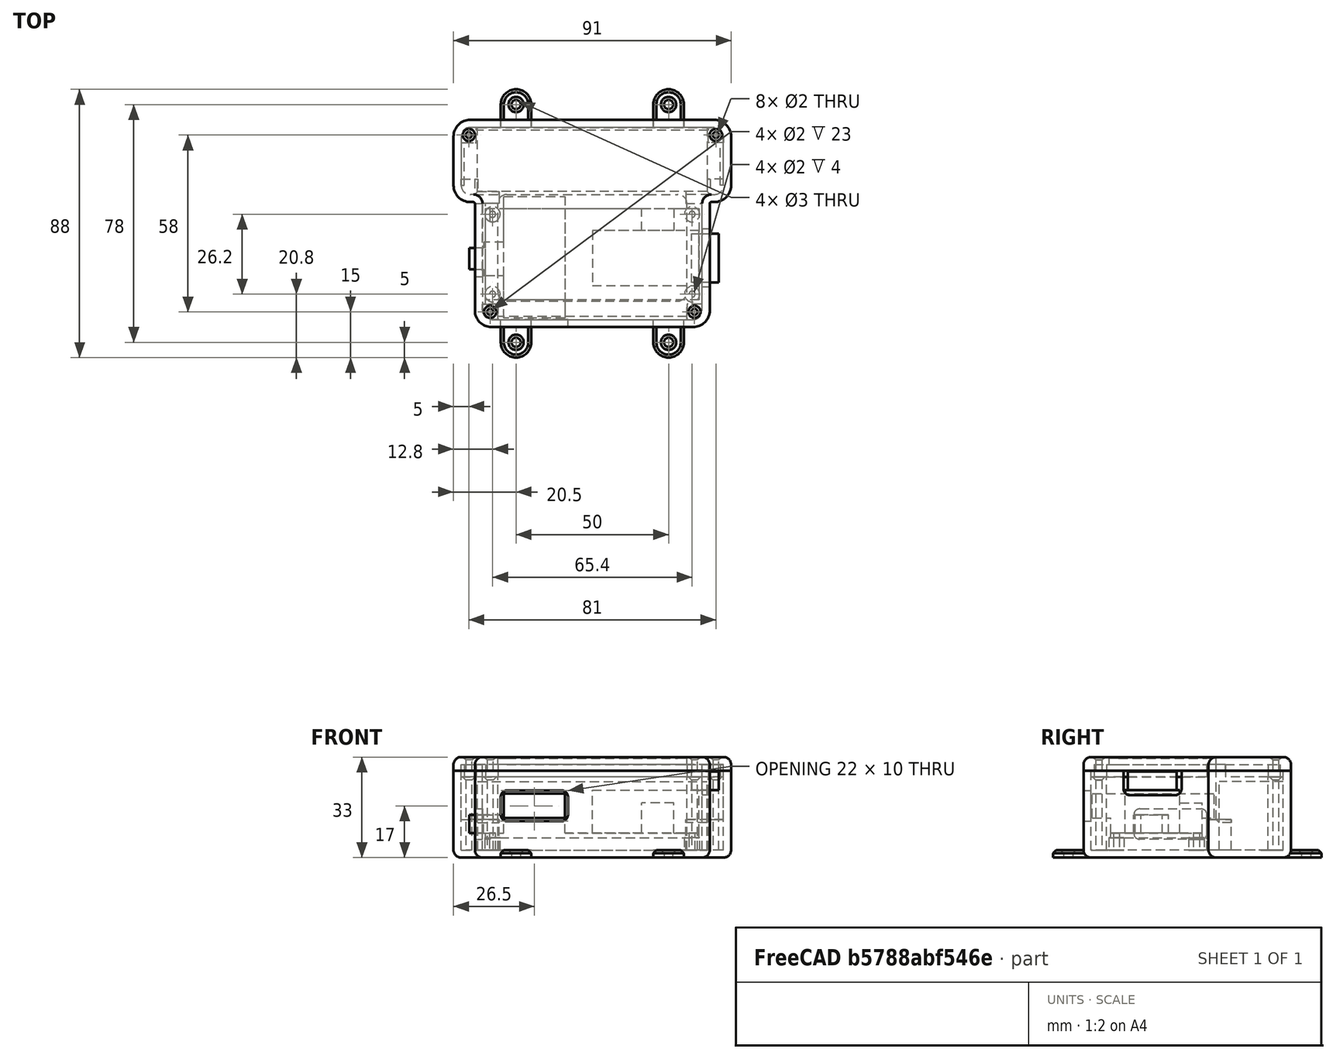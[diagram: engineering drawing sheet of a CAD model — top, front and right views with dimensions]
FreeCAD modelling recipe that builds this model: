
FCSTD DOCUMENT  (FreeCAD 0.18R16110 (Git))
Label: Boitier_elec_V1
License: All rights reserved
LicenseURL: http://en.wikipedia.org/wiki/All_rights_reserved
objects: Sketcher::SketchObject×21, PartDesign::Pad×16, PartDesign::Fillet×5, PartDesign::Pocket×5, PartDesign::Body×4, PartDesign::Chamfer×4, PartDesign::Thickness×2, Mesh::Feature×2
note: 78 computed .brp shape members not serialized (recipe doc carries the construction recipe); baked Part::Feature solids carry a one-line shape summary decoded from their .brp

FEATURE [Sketcher::SketchObject] Sketch
  MapMode = 5
  Support = -> [XY_Plane]
  sketch-geometry (8):
    g0: LineSegment StartX=-43 StartY=22 StartZ=0 EndX=-43 EndY=0 EndZ=0
    g1: LineSegment StartX=-43 StartY=0 StartZ=0 EndX=-36 EndY=0 EndZ=0
    g2: LineSegment StartX=-36 StartY=0 StartZ=0 EndX=-36 EndY=-41 EndZ=0
    g3: LineSegment StartX=-36 StartY=-41 StartZ=0 EndX=36 EndY=-41 EndZ=0
    g4: LineSegment StartX=36 StartY=-41 StartZ=0 EndX=36 EndY=0 EndZ=0
    g5: LineSegment StartX=36 StartY=0 StartZ=0 EndX=43 EndY=0 EndZ=0
    g6: LineSegment StartX=43 StartY=0 StartZ=0 EndX=43 EndY=22 EndZ=0
    g7: LineSegment StartX=43 StartY=22 StartZ=0 EndX=-43 EndY=22 EndZ=0
  constraints (22):
    c: Vertical(g0)
    c: Coincident(g0,g1)
    c: Horizontal(g1)
    c: Coincident(g1,g2)
    c: Vertical(g2)
    c: Coincident(g2,g3)
    c: Coincident(g3,g4)
    c: Vertical(g4)
    c: Coincident(g4,g5)
    c: Horizontal(g5)
    c: Coincident(g5,g6)
    c: Vertical(g6)
    c: Coincident(g6,g7)
    c: Coincident(g7,g0)
    c: Symmetric(g0,g6,g-2)
    c: Symmetric(g2,g3,g-2)
    c: DistanceX(g3,g3) = 72
    c: DistanceY(g4,g4) = 41
    c: Equal(g2,g4)
    c: DistanceX(g7,g7) = 86
    c: DistanceY(g6,g6) = 22
    c: PointOnObject(g1,g-1)
FEATURE [PartDesign::Pad] Pad  label="Contours_boite"
  Length = 26
  Length2 = 100
  Profile = -> Sketch
  Type = 0
FEATURE [PartDesign::Fillet] Fillet
  Base = -> Pad [Edge8,Edge11,Edge17,Edge2,Edge1,Edge20,Edge14,Edge5]
  BaseFeature = -> Pad
  Radius = 3
FEATURE [PartDesign::Thickness] Thickness
  Base = -> Fillet [Face5]
  BaseFeature = -> Fillet
  Join = 0
  Mode = 0
  Value = 2.5
FEATURE [Sketcher::SketchObject] Sketch001
  ExternalGeometry = -> [Thickness]
  MapMode = 5
  Support = -> [Thickness]
  sketch-geometry (8):
    g0: Circle CenterX=-32.7 CenterY=-6.5 CenterZ=0 NormalX=0 NormalY=0 NormalZ=1 AngleXU=0 Radius=1
    g1: Circle CenterX=-32.7 CenterY=-32.7 CenterZ=0 NormalX=0 NormalY=0 NormalZ=1 AngleXU=0 Radius=1
    g2: Circle CenterX=32.7 CenterY=-6.5 CenterZ=0 NormalX=0 NormalY=0 NormalZ=1 AngleXU=0 Radius=1
    g3: Circle CenterX=32.7 CenterY=-32.7 CenterZ=0 NormalX=0 NormalY=0 NormalZ=1 AngleXU=0 Radius=1
    g4: Circle CenterX=-32.7 CenterY=-6.5 CenterZ=0 NormalX=0 NormalY=0 NormalZ=1 AngleXU=0 Radius=2.5
    g5: Circle CenterX=-32.7 CenterY=-32.7 CenterZ=0 NormalX=0 NormalY=0 NormalZ=1 AngleXU=0 Radius=2.5
    g6: Circle CenterX=32.7 CenterY=-32.7 CenterZ=0 NormalX=0 NormalY=0 NormalZ=1 AngleXU=0 Radius=2.5
    g7: Circle CenterX=32.7 CenterY=-6.5 CenterZ=0 NormalX=0 NormalY=0 NormalZ=1 AngleXU=0 Radius=2.5
  constraints (18):
    c: Symmetric(g0,g2,g-2)
    c: Symmetric(g1,g3,g-2)
    c: Radius(g0) = 1
    c: Equal(g0,g2)
    c: Equal(g0,g3)
    c: Equal(g0,g1)
    c: Distance(g1,g-4) = 8.3
    c: Distance(g0,g-4) = 34.5
    c: Distance(g1,g3) = 65.4
    c: Distance(g0,g2) = 65.4
    c: Coincident(g5,g1)
    c: Coincident(g6,g3)
    c: Coincident(g7,g2)
    c: Radius(g7) = 2.5
    c: Equal(g7,g6)
    c: Equal(g7,g4)
    c: Equal(g7,g5)
    c: Coincident(g4,g0)
FEATURE [PartDesign::Pad] Pad001  label="Piliers_fixation_PCB"
  BaseFeature = -> Thickness
  Length = 4
  Length2 = 100
  Profile = -> Sketch001
  Type = 0
FEATURE [Sketcher::SketchObject] Sketch002
  MapMode = 5
  Support = -> [XY_Plane001]
  sketch-geometry (8):
    g0: LineSegment StartX=-35 StartY=15 StartZ=0 EndX=35 EndY=15 EndZ=0
    g1: LineSegment StartX=35 StartY=15 StartZ=0 EndX=35 EndY=-15 EndZ=0
    g2: LineSegment StartX=35 StartY=-15 StartZ=0 EndX=-35 EndY=-15 EndZ=0
    g3: LineSegment StartX=-35 StartY=-15 StartZ=0 EndX=-35 EndY=15 EndZ=0
    g4: Circle CenterX=-32.7 CenterY=13.1 CenterZ=0 NormalX=0 NormalY=0 NormalZ=1 AngleXU=0 Radius=1
    g5: Circle CenterX=-32.7 CenterY=-13.1 CenterZ=0 NormalX=0 NormalY=0 NormalZ=1 AngleXU=0 Radius=1
    g6: Circle CenterX=32.7 CenterY=13.1 CenterZ=0 NormalX=0 NormalY=0 NormalZ=1 AngleXU=0 Radius=1
    g7: Circle CenterX=32.7 CenterY=-13.1 CenterZ=0 NormalX=0 NormalY=0 NormalZ=1 AngleXU=0 Radius=1
  constraints (19):
    c: Coincident(g0,g1)
    c: Coincident(g1,g2)
    c: Coincident(g2,g3)
    c: Coincident(g3,g0)
    c: Horizontal(g2)
    c: Vertical(g1)
    c: DistanceY(g1,g1) = 30
    c: DistanceX(g0,g0) = 70
    c: Symmetric(g0,g0,g-2)
    c: Radius(g4) = 1
    c: Equal(g4,g5)
    c: Equal(g4,g6)
    c: Equal(g4,g7)
    c: Distance(g4,g5) = 26.2
    c: Symmetric(g4,g6,g-2)
    c: Distance(g4,g6) = 65.4
    c: Symmetric(g5,g7,g-2)
    c: Symmetric(g2,g0,g-1)
    c: Symmetric(g7,g6,g-1)
FEATURE [PartDesign::Pad] Pad002
  Length = 1.5
  Length2 = 100
  Profile = -> Sketch002
  Type = 0
FEATURE [Sketcher::SketchObject] Sketch003
  ExternalGeometry = -> [Pad002]
  MapMode = 5
  Placement = pos=(0,0,1.5) rot=(0,0,1;0rad)
  Support = -> [Pad002]
  sketch-geometry (4):
    g0: LineSegment StartX=-29 StartY=15 StartZ=0 EndX=-9 EndY=15 EndZ=0
    g1: LineSegment StartX=-9 StartY=15 StartZ=0 EndX=-9 EndY=-15 EndZ=0
    g2: LineSegment StartX=-9 StartY=-15 StartZ=0 EndX=-29 EndY=-15 EndZ=0
    g3: LineSegment StartX=-29 StartY=-15 StartZ=0 EndX=-29 EndY=15 EndZ=0
  constraints (12):
    c: Coincident(g0,g1)
    c: Coincident(g1,g2)
    c: Coincident(g2,g3)
    c: Coincident(g3,g0)
    c: Horizontal(g0)
    c: Horizontal(g2)
    c: Vertical(g1)
    c: Vertical(g3)
    c: PointOnObject(g0,g-4)
    c: PointOnObject(g1,g-5)
    c: DistanceX(g2,g2) = 20
    c: Distance(g0,g-3) = 6
FEATURE [PartDesign::Pad] Pad003
  BaseFeature = -> Pad002
  Length = 5
  Length2 = 100
  Profile = -> Sketch003
  Type = 0
FEATURE [Sketcher::SketchObject] Sketch004
  ExternalGeometry = -> [Pad003]
  MapMode = 5
  Placement = pos=(0,0,6.5) rot=(0,0,1;0rad)
  Support = -> [Pad003]
  sketch-geometry (4):
    g0: LineSegment StartX=-29 StartY=19 StartZ=0 EndX=-9 EndY=19 EndZ=0
    g1: LineSegment StartX=-9 StartY=19 StartZ=0 EndX=-9 EndY=-21 EndZ=0
    g2: LineSegment StartX=-9 StartY=-21 StartZ=0 EndX=-29 EndY=-21 EndZ=0
    g3: LineSegment StartX=-29 StartY=-21 StartZ=0 EndX=-29 EndY=19 EndZ=0
  constraints (12):
    c: Coincident(g0,g1)
    c: Coincident(g1,g2)
    c: Coincident(g2,g3)
    c: Coincident(g3,g0)
    c: Horizontal(g0)
    c: Horizontal(g2)
    c: Vertical(g1)
    c: Vertical(g3)
    c: PointOnObject(g-6,g1)
    c: PointOnObject(g-4,g3)
    c: DistanceY(g1,g1) = 40
    c: Distance(g2,g-5) = 6
FEATURE [PartDesign::Pad] Pad004
  BaseFeature = -> Pad003
  Length = 8
  Length2 = 100
  Profile = -> Sketch004
  Type = 0
FEATURE [Sketcher::SketchObject] Sketch005
  ExternalGeometry = -> [Pad004]
  MapMode = 5
  Placement = pos=(0,0,1.5) rot=(0,0,1;0rad)
  Support = -> [Pad004]
  sketch-geometry (4):
    g0: LineSegment StartX=35 StartY=7.7 StartZ=0 EndX=0 EndY=7.7 EndZ=0
    g1: LineSegment StartX=0 StartY=7.7 StartZ=0 EndX=0 EndY=-10.3 EndZ=0
    g2: LineSegment StartX=0 StartY=-10.3 StartZ=0 EndX=35 EndY=-10.3 EndZ=0
    g3: LineSegment StartX=35 StartY=-10.3 StartZ=0 EndX=35 EndY=7.7 EndZ=0
  constraints (12):
    c: Coincident(g0,g1)
    c: Coincident(g1,g2)
    c: Coincident(g2,g3)
    c: Coincident(g3,g0)
    c: Horizontal(g0)
    c: Horizontal(g2)
    c: Vertical(g1)
    c: Vertical(g3)
    c: PointOnObject(g0,g-4)
    c: DistanceY(g3,g3) = 18
    c: DistanceX(g2,g2) = 35
    c: Distance(g1,g-5) = 4.7
FEATURE [PartDesign::Pad] Pad005
  BaseFeature = -> Pad004
  Length = 14.2
  Length2 = 100
  Profile = -> Sketch005
  Type = 0
FEATURE [Sketcher::SketchObject] Sketch006
  ExternalGeometry = -> [Pad005]
  MapMode = 5
  Placement = pos=(0,0,15.7) rot=(0,0,1;0rad)
  Support = -> [Pad005]
  sketch-geometry (4):
    g0: LineSegment StartX=32.5 StartY=6.7 StartZ=0 EndX=41.5 EndY=6.7 EndZ=0
    g1: LineSegment StartX=41.5 StartY=6.7 StartZ=0 EndX=41.5 EndY=-9.3 EndZ=0
    g2: LineSegment StartX=41.5 StartY=-9.3 StartZ=0 EndX=32.5 EndY=-9.3 EndZ=0
    g3: LineSegment StartX=32.5 StartY=-9.3 StartZ=0 EndX=32.5 EndY=6.7 EndZ=0
  constraints (12):
    c: Coincident(g0,g1)
    c: Coincident(g1,g2)
    c: Coincident(g2,g3)
    c: Coincident(g3,g0)
    c: Horizontal(g0)
    c: Horizontal(g2)
    c: Vertical(g1)
    c: Vertical(g3)
    c: DistanceY(g3,g3) = 16
    c: Distance(g0,g-3) = 1
    c: Distance(g0,g-5) = 2.5
    c: DistanceX(g2,g2) = 9
FEATURE [PartDesign::Pad] Pad006
  BaseFeature = -> Pad005
  Length = 6
  Length2 = 100
  Profile = -> Sketch006
  Type = 0
FEATURE [Sketcher::SketchObject] Sketch007
  ExternalGeometry = -> [Pad001]
  MapMode = 5
  Placement = pos=(38.5,0,0) rot=(0.57735,0.57735,0.57735;2.0944rad)
  Support = -> [Pad001]
  sketch-geometry (4):
    g0: LineSegment StartX=-30.35 StartY=26 StartZ=0 EndX=-11.35 EndY=26 EndZ=0
    g1: LineSegment StartX=-11.35 StartY=26 StartZ=0 EndX=-11.35 EndY=18 EndZ=0
    g2: LineSegment StartX=-11.35 StartY=18 StartZ=0 EndX=-30.35 EndY=18 EndZ=0
    g3: LineSegment StartX=-30.35 StartY=18 StartZ=0 EndX=-30.35 EndY=26 EndZ=0
  constraints (12):
    c: Coincident(g0,g1)
    c: Coincident(g1,g2)
    c: Coincident(g2,g3)
    c: Coincident(g3,g0)
    c: Horizontal(g0)
    c: Horizontal(g2)
    c: Vertical(g1)
    c: Vertical(g3)
    c: PointOnObject(g0,g-3)
    c: DistanceX(g2,g2) = 19
    c: DistanceY(g3,g3) = 8
    c: Distance(g0,g-4) = 7.65
FEATURE [PartDesign::Pocket] Pocket  label="Passage_fils_prog"
  BaseFeature = -> Pad001
  Length = 5
  Length2 = 100
  Profile = -> Sketch007
  Type = 0
FEATURE [Sketcher::SketchObject] Sketch008
  MapMode = 5
  Support = -> [XY_Plane002]
  sketch-geometry (4):
    g0: LineSegment StartX=-37.625 StartY=22 StartZ=0 EndX=37.625 EndY=22 EndZ=0
    g1: LineSegment StartX=37.625 StartY=22 StartZ=0 EndX=37.625 EndY=1 EndZ=0
    g2: LineSegment StartX=37.625 StartY=1 StartZ=0 EndX=-37.625 EndY=1 EndZ=0
    g3: LineSegment StartX=-37.625 StartY=1 StartZ=0 EndX=-37.625 EndY=22 EndZ=0
  constraints (11):
    c: Coincident(g0,g1)
    c: Coincident(g1,g2)
    c: Coincident(g2,g3)
    c: Coincident(g3,g0)
    c: Horizontal(g2)
    c: Vertical(g1)
    c: Vertical(g3)
    c: Symmetric(g0,g0,g-2)
    c: DistanceY(g1,g1) = 21
    c: DistanceX(g0,g0) = 75.25
    c: DistanceY(g-1,g0) = 22
FEATURE [PartDesign::Pad] Pad007
  Length = 22.5
  Length2 = 100
  Profile = -> Sketch008
  Type = 0
FEATURE [PartDesign::Body] Body002  label="Porte_batterie"
  Group = -> [Sketch008,Pad007]
  Origin = -> Origin002
  Tip = -> Pad007
FEATURE [Sketcher::SketchObject] Sketch009
  ExternalGeometry = -> [Pocket]
  MapMode = 5
  Support = -> [Pocket]
  sketch-geometry (14):
    g0: LineSegment StartX=43 StartY=5 StartZ=0 EndX=37.6 EndY=5 EndZ=0
    g1: LineSegment StartX=37.6 StartY=5 StartZ=0 EndX=37.6 EndY=1 EndZ=0
    g2: LineSegment StartX=37.6 StartY=1 StartZ=0 EndX=30.6 EndY=1 EndZ=0
    g3: LineSegment StartX=30.6 StartY=1 StartZ=0 EndX=30.6 EndY=-3 EndZ=0
    g4: LineSegment StartX=30.6 StartY=-3 StartZ=0 EndX=37.6 EndY=-3 EndZ=0
    g5: LineSegment StartX=37.6 StartY=-3 StartZ=0 EndX=43 EndY=0 EndZ=0
    g6: LineSegment StartX=43 StartY=0 StartZ=0 EndX=43 EndY=5 EndZ=0
    g7: LineSegment StartX=-43 StartY=5 StartZ=0 EndX=-37.6 EndY=5 EndZ=0
    g8: LineSegment StartX=-37.6 StartY=5 StartZ=0 EndX=-37.6 EndY=1 EndZ=0
    g9: LineSegment StartX=-37.6 StartY=1 StartZ=0 EndX=-30.6 EndY=1 EndZ=0
    g10: LineSegment StartX=-30.6 StartY=1 StartZ=0 EndX=-30.6 EndY=-3 EndZ=0
    g11: LineSegment StartX=-30.6 StartY=-3 StartZ=0 EndX=-37.6 EndY=-3 EndZ=0
    g12: LineSegment StartX=-37.6 StartY=-3 StartZ=0 EndX=-43 EndY=0 EndZ=0
    g13: LineSegment StartX=-43 StartY=0 StartZ=0 EndX=-43 EndY=5 EndZ=0
  constraints (37):
    c: Horizontal(g0)
    c: Coincident(g0,g1)
    c: Vertical(g1)
    c: Coincident(g1,g2)
    c: Horizontal(g2)
    c: Coincident(g2,g3)
    c: Vertical(g3)
    c: Coincident(g3,g4)
    c: Horizontal(g4)
    c: Coincident(g4,g5)
    c: PointOnObject(g5,g-1)
    c: Coincident(g5,g6)
    c: Coincident(g6,g0)
    c: Vertical(g6)
    c: DistanceY(g3,g3) = 4
    c: DistanceX(g2,g2) = 7
    c: DistanceX(g0,g0) = 5.4
    c: DistanceY(g1,g1) = 4
    c: Distance(g0,g-1) = 5
    c: DistanceX(g4,g4) = 7
    c: PointOnObject(g0,g-5)
    c: Coincident(g7,g8)
    c: Coincident(g8,g9)
    c: Horizontal(g9)
    c: Coincident(g9,g10)
    c: Vertical(g10)
    c: Coincident(g10,g11)
    c: Coincident(g11,g12)
    c: PointOnObject(g12,g-1)
    c: Coincident(g12,g13)
    c: Coincident(g13,g7)
    c: Vertical(g13)
    c: Symmetric(g7,g0,g-2)
    c: Symmetric(g7,g0,g-2)
    c: Symmetric(g8,g1,g-2)
    c: Symmetric(g10,g3,g-2)
    c: Symmetric(g11,g4,g-2)
FEATURE [PartDesign::Pad] Pad008  label="Maintiens_batterie"
  BaseFeature = -> Pocket
  Length = 10
  Length2 = 100
  Profile = -> Sketch009
  Type = 0
FEATURE [Sketcher::SketchObject] Sketch010
  ExternalGeometry = -> [Pad006]
  MapMode = 5
  Placement = pos=(0,0,1.5) rot=(0,0,1;0rad)
  Support = -> [Pad006]
  sketch-geometry (4):
    g0: LineSegment StartX=16.2 StartY=15 StartZ=0 EndX=26.7 EndY=15 EndZ=0
    g1: LineSegment StartX=26.7 StartY=15 StartZ=0 EndX=26.7 EndY=7.7 EndZ=0
    g2: LineSegment StartX=26.7 StartY=7.7 StartZ=0 EndX=16.2 EndY=7.7 EndZ=0
    g3: LineSegment StartX=16.2 StartY=7.7 StartZ=0 EndX=16.2 EndY=15 EndZ=0
  constraints (12):
    c: Coincident(g0,g1)
    c: Coincident(g1,g2)
    c: Coincident(g2,g3)
    c: Coincident(g3,g0)
    c: Horizontal(g0)
    c: Horizontal(g2)
    c: Vertical(g1)
    c: Vertical(g3)
    c: PointOnObject(g0,g-3)
    c: PointOnObject(g1,g-5)
    c: Distance(g0,g-4) = 8.3
    c: DistanceX(g0,g0) = 10.5
FEATURE [PartDesign::Pad] Pad009
  BaseFeature = -> Pad006
  Length = 10
  Length2 = 100
  Profile = -> Sketch010
  Type = 0
FEATURE [Sketcher::SketchObject] Sketch012
  ExternalGeometry = -> [Pad009]
  MapMode = 5
  Placement = pos=(0,0,1.5) rot=(0,0,1;0rad)
  Support = -> [Pad009]
  sketch-geometry (8):
    g0: LineSegment StartX=-29 StartY=4 StartZ=0 EndX=-35.7 EndY=4 EndZ=0
    g1: LineSegment StartX=-35.7 StartY=4 StartZ=0 EndX=-35.7 EndY=2 EndZ=0
    g2: LineSegment StartX=-35.7 StartY=2 StartZ=0 EndX=-40.4 EndY=2 EndZ=0
    g3: LineSegment StartX=-40.4 StartY=2 StartZ=0 EndX=-40.4 EndY=-5 EndZ=0
    g4: LineSegment StartX=-40.4 StartY=-5 StartZ=0 EndX=-35.7 EndY=-5 EndZ=0
    g5: LineSegment StartX=-35.7 StartY=-5 StartZ=0 EndX=-35.7 EndY=-7 EndZ=0
    g6: LineSegment StartX=-35.7 StartY=-7 StartZ=0 EndX=-29 EndY=-7 EndZ=0
    g7: LineSegment StartX=-29 StartY=-7 StartZ=0 EndX=-29 EndY=4 EndZ=0
  constraints (24):
    c: PointOnObject(g0,g-6)
    c: Horizontal(g0)
    c: Coincident(g0,g1)
    c: Vertical(g1)
    c: Coincident(g1,g2)
    c: Horizontal(g2)
    c: Coincident(g2,g3)
    c: Vertical(g3)
    c: Coincident(g3,g4)
    c: Horizontal(g4)
    c: Coincident(g4,g5)
    c: Vertical(g5)
    c: Coincident(g5,g6)
    c: Horizontal(g6)
    c: Coincident(g6,g7)
    c: Coincident(g7,g0)
    c: Vertical(g7)
    c: DistanceX(g0,g0) = 6.7
    c: Equal(g0,g6)
    c: DistanceX(g2,g2) = 4.7
    c: DistanceY(g3,g3) = 7
    c: DistanceY(g5,g5) = 2
    c: Equal(g5,g1)
    c: Distance(g5,g-5) = 8
FEATURE [PartDesign::Pad] Pad010
  BaseFeature = -> Pad009
  Length = 6
  Length2 = 100
  Profile = -> Sketch012
  Type = 0
FEATURE [PartDesign::Body] Body001  label="PCB"
  Group = -> [Sketch002,Pad002,Sketch003,Pad003,Sketch004,Pad004,Sketch005,Pad005,Sketch006,Pad006,Sketch010,Pad009,Sketch012,Pad010]
  Origin = -> Origin001
  Placement = pos=(0,-19.6,4) rot=(0,0,1;0rad)
  Tip = -> Pad010
FEATURE [Sketcher::SketchObject] Sketch013
  MapMode = 5
  Placement = pos=(0,-43.5,0) rot=(1,0,0;1.5708rad)
  sketch-geometry (4):
    g0: LineSegment StartX=-30 StartY=19.5 StartZ=0 EndX=-8 EndY=19.5 EndZ=0
    g1: LineSegment StartX=-8 StartY=19.5 StartZ=0 EndX=-8 EndY=9.5 EndZ=0
    g2: LineSegment StartX=-8 StartY=9.5 StartZ=0 EndX=-30 EndY=9.5 EndZ=0
    g3: LineSegment StartX=-30 StartY=9.5 StartZ=0 EndX=-30 EndY=19.5 EndZ=0
  constraints (11):
    c: Coincident(g0,g1)
    c: Coincident(g1,g2)
    c: Coincident(g2,g3)
    c: Coincident(g3,g0)
    c: Horizontal(g0)
    c: Horizontal(g2)
    c: Vertical(g1)
    c: Vertical(g3)
    c: DistanceX(g2,g2) = 22
    c: DistanceY(g3,g3) = 10
    c: DistanceY(g-1,g2) = 9.5
FEATURE [PartDesign::Pocket] Pocket002  label="Passage_solar_usb"
  BaseFeature = -> Pad008
  Length = 5
  Length2 = 100
  Profile = -> Sketch013
  Type = 0
FEATURE [Sketcher::SketchObject] Sketch014
  ExternalGeometry = -> [Pocket002]
  MapMode = 5
  Placement = pos=(-38.5,0,0) rot=(0.57735,-0.57735,-0.57735;2.0944rad)
  Support = -> [Pocket002]
  sketch-geometry (4):
    g0: LineSegment StartX=3 StartY=13.5 StartZ=0 EndX=27 EndY=13.5 EndZ=0
    g1: LineSegment StartX=27 StartY=13.5 StartZ=0 EndX=27 EndY=3.5 EndZ=0
    g2: LineSegment StartX=27 StartY=3.5 StartZ=0 EndX=3 EndY=3.5 EndZ=0
    g3: LineSegment StartX=3 StartY=3.5 StartZ=0 EndX=3 EndY=13.5 EndZ=0
  constraints (12):
    c: Coincident(g0,g1)
    c: Coincident(g1,g2)
    c: Coincident(g2,g3)
    c: Coincident(g3,g0)
    c: Horizontal(g0)
    c: Horizontal(g2)
    c: Vertical(g1)
    c: Vertical(g3)
    c: PointOnObject(g0,g-3)
    c: DistanceX(g0,g0) = 24
    c: DistanceY(g1,g1) = 10
    c: DistanceY(g-1,g1) = 3.5
FEATURE [PartDesign::Pocket] Pocket003  label="Passage_fils_interrupteur"
  BaseFeature = -> Pocket002
  Length = 5
  Length2 = 100
  Profile = -> Sketch014
  Type = 0
FEATURE [PartDesign::Fillet] Fillet001
  Base = -> Pocket003 [Edge185,Edge187,Edge184,Edge186]
  BaseFeature = -> Pocket003
  Radius = 2
FEATURE [PartDesign::Fillet] Fillet002
  Base = -> Fillet001 [Edge205,Edge206,Edge204,Edge203]
  BaseFeature = -> Fillet001
  Radius = 2
FEATURE [PartDesign::Fillet] Fillet003
  Base = -> Fillet002 [Edge157,Edge200]
  BaseFeature = -> Fillet002
  Radius = 2
FEATURE [Sketcher::SketchObject] Sketch015
  ExternalGeometry = -> [Fillet003]
  MapMode = 5
  Support = -> [Fillet003]
  sketch-geometry (20):
    g0: LineSegment StartX=-43 StartY=17 StartZ=0 EndX=-38 EndY=17 EndZ=0
    g1: LineSegment StartX=-38 StartY=17 StartZ=0 EndX=-38 EndY=22 EndZ=0
    g2: LineSegment StartX=-38 StartY=22 StartZ=0 EndX=-43 EndY=22 EndZ=0
    g3: LineSegment StartX=-43 StartY=22 StartZ=0 EndX=-43 EndY=17 EndZ=0
    g4: Circle CenterX=-40.5 CenterY=19.5 CenterZ=0 NormalX=0 NormalY=0 NormalZ=1 AngleXU=0 Radius=1
    g5: LineSegment StartX=43 StartY=17 StartZ=0 EndX=38 EndY=17 EndZ=0
    g6: LineSegment StartX=38 StartY=17 StartZ=0 EndX=38 EndY=22 EndZ=0
    g7: LineSegment StartX=38 StartY=22 StartZ=0 EndX=43 EndY=22 EndZ=0
    g8: LineSegment StartX=43 StartY=22 StartZ=0 EndX=43 EndY=17 EndZ=0
    g9: Circle CenterX=40.5 CenterY=19.5 CenterZ=0 NormalX=0 NormalY=0 NormalZ=1 AngleXU=0 Radius=1
    g10: LineSegment StartX=31 StartY=-41 StartZ=0 EndX=36 EndY=-41 EndZ=0
    g11: LineSegment StartX=36 StartY=-41 StartZ=0 EndX=36 EndY=-36 EndZ=0
    g12: LineSegment StartX=36 StartY=-36 StartZ=0 EndX=31 EndY=-36 EndZ=0
    g13: LineSegment StartX=31 StartY=-36 StartZ=0 EndX=31 EndY=-41 EndZ=0
    g14: LineSegment StartX=-36 StartY=-36 StartZ=0 EndX=-31 EndY=-36 EndZ=0
    g15: LineSegment StartX=-31 StartY=-36 StartZ=0 EndX=-31 EndY=-41 EndZ=0
    g16: LineSegment StartX=-31 StartY=-41 StartZ=0 EndX=-36 EndY=-41 EndZ=0
    g17: LineSegment StartX=-36 StartY=-41 StartZ=0 EndX=-36 EndY=-36 EndZ=0
    g18: Circle CenterX=-33.5 CenterY=-38.5 CenterZ=0 NormalX=0 NormalY=0 NormalZ=1 AngleXU=0 Radius=1
    g19: Circle CenterX=33.5 CenterY=-38.5 CenterZ=0 NormalX=0 NormalY=0 NormalZ=1 AngleXU=0 Radius=1
  constraints (60):
    c: Coincident(g0,g1)
    c: Coincident(g1,g2)
    c: Coincident(g2,g3)
    c: Coincident(g3,g0)
    c: Horizontal(g0)
    c: Horizontal(g2)
    c: Vertical(g1)
    c: Vertical(g3)
    c: PointOnObject(g0,g-3)
    c: PointOnObject(g1,g-4)
    c: DistanceX(g0,g0) = 5
    c: DistanceY(g1,g1) = 5
    c: Distance(g4,g3) = 2.5
    c: Distance(g4,g2) = 2.5
    c: Coincident(g5,g6)
    c: Coincident(g6,g7)
    c: Coincident(g7,g8)
    c: Coincident(g8,g5)
    c: Horizontal(g5)
    c: Horizontal(g7)
    c: Vertical(g6)
    c: Vertical(g8)
    c: PointOnObject(g5,g-5)
    c: PointOnObject(g6,g-4)
    c: DistanceY(g8,g8) = 5
    c: DistanceX(g5,g5) = 5
    c: Distance(g9,g8) = 2.5
    c: Distance(g9,g7) = 2.5
    c: Coincident(g10,g11)
    c: Coincident(g11,g12)
    c: Coincident(g12,g13)
    c: Coincident(g13,g10)
    c: Horizontal(g10)
    c: Horizontal(g12)
    c: Vertical(g11)
    c: Vertical(g13)
    c: PointOnObject(g10,g-6)
    c: PointOnObject(g11,g-8)
    c: DistanceY(g13,g13) = 5
    c: DistanceX(g12,g12) = 5
    c: Coincident(g14,g15)
    c: Coincident(g15,g16)
    c: Coincident(g16,g17)
    c: Coincident(g17,g14)
    c: Horizontal(g14)
    c: Horizontal(g16)
    c: Vertical(g15)
    c: Vertical(g17)
    c: PointOnObject(g14,g-7)
    c: PointOnObject(g15,g-6)
    c: DistanceY(g15,g15) = 5
    c: DistanceX(g14,g14) = 5
    c: Distance(g18,g16) = 2.5
    c: Distance(g18,g17) = 2.5
    c: Distance(g19,g10) = 2.5
    c: Distance(g19,g11) = 2.5
    c: Radius(g19) = 1
    c: Equal(g19,g9)
    c: Equal(g19,g4)
    c: Equal(g19,g18)
FEATURE [PartDesign::Pad] Pad011
  BaseFeature = -> Fillet003
  Length = 24
  Length2 = 100
  Profile = -> Sketch015
  Type = 0
FEATURE [Sketcher::SketchObject] Sketch016
  ExternalGeometry = -> [Pad011]
  MapMode = 5
  Placement = pos=(0,0,-2.5) rot=(1,0,0;3.14159rad)
  Support = -> [Pad011]
  sketch-geometry (20):
    g0: ArcOfCircle CenterX=-25 CenterY=48.5 CenterZ=0 NormalX=0 NormalY=0 NormalZ=1 AngleXU=0 Radius=5 StartAngle=-1.2159e-12 EndAngle=3.14159
    g1: ArcOfCircle CenterX=-25 CenterY=38.5 CenterZ=0 NormalX=0 NormalY=0 NormalZ=1 AngleXU=0 Radius=5 StartAngle=3.14159 EndAngle=6.28319
    g2: LineSegment StartX=-30 StartY=48.5 StartZ=0 EndX=-30 EndY=38.5 EndZ=0
    g3: LineSegment StartX=-20 StartY=48.5 StartZ=0 EndX=-20 EndY=38.5 EndZ=0
    g4: Circle CenterX=-25 CenterY=48.5 CenterZ=0 NormalX=0 NormalY=0 NormalZ=1 AngleXU=0 Radius=1.5
    g5: ArcOfCircle CenterX=25 CenterY=48.5 CenterZ=0 NormalX=0 NormalY=0 NormalZ=1 AngleXU=0 Radius=5 StartAngle=1.00045e-11 EndAngle=3.14159
    g6: ArcOfCircle CenterX=25 CenterY=38.5 CenterZ=0 NormalX=0 NormalY=0 NormalZ=1 AngleXU=0 Radius=5 StartAngle=3.14159 EndAngle=6.28319
    g7: LineSegment StartX=20 StartY=48.5 StartZ=0 EndX=20 EndY=38.5 EndZ=0
    g8: LineSegment StartX=30 StartY=48.5 StartZ=0 EndX=30 EndY=38.5 EndZ=0
    g9: Circle CenterX=25 CenterY=48.5 CenterZ=0 NormalX=0 NormalY=0 NormalZ=1 AngleXU=0 Radius=1.5
    g10: ArcOfCircle CenterX=-25 CenterY=-19.5 CenterZ=0 NormalX=0 NormalY=0 NormalZ=1 AngleXU=0 Radius=5 StartAngle=6.867e-13 EndAngle=3.14159
    g11: ArcOfCircle CenterX=-25 CenterY=-29.5 CenterZ=0 NormalX=0 NormalY=0 NormalZ=1 AngleXU=0 Radius=5 StartAngle=3.14159 EndAngle=6.28319
    g12: LineSegment StartX=-30 StartY=-19.5 StartZ=0 EndX=-30 EndY=-29.5 EndZ=0
    g13: LineSegment StartX=-20 StartY=-19.5 StartZ=0 EndX=-20 EndY=-29.5 EndZ=0
    g14: ArcOfCircle CenterX=25 CenterY=-19.5 CenterZ=0 NormalX=0 NormalY=0 NormalZ=1 AngleXU=0 Radius=5 StartAngle=5e-16 EndAngle=3.14159
    g15: ArcOfCircle CenterX=25 CenterY=-29.5 CenterZ=0 NormalX=0 NormalY=0 NormalZ=1 AngleXU=0 Radius=5 StartAngle=3.14159 EndAngle=6.28319
    g16: LineSegment StartX=20 StartY=-19.5 StartZ=0 EndX=20 EndY=-29.5 EndZ=0
    g17: LineSegment StartX=30 StartY=-19.5 StartZ=0 EndX=30 EndY=-29.5 EndZ=0
    g18: Circle CenterX=-25 CenterY=-29.5 CenterZ=0 NormalX=0 NormalY=0 NormalZ=1 AngleXU=0 Radius=1.5
    g19: Circle CenterX=25 CenterY=-29.5 CenterZ=0 NormalX=0 NormalY=0 NormalZ=1 AngleXU=0 Radius=1.5
  constraints (42):
    c: Tangent(g0,g3) = 1.5708
    c: Tangent(g0,g2) = -1.5708
    c: Tangent(g2,g1) = -1.5708
    c: Tangent(g3,g1) = 1.5708
    c: Vertical(g2)
    c: Coincident(g4,g0)
    c: Radius(g4) = 1.5
    c: Radius(g0) = 5
    c: Distance(g0,g-4) = 5
    c: Symmetric(g0,g1,g-4)
    c: DistanceX(g-2,g0) = -25
    c: Tangent(g5,g8) = 1.5708
    c: Tangent(g5,g7) = -1.5708
    c: Tangent(g7,g6) = -1.5708
    c: Tangent(g8,g6) = 1.5708
    c: Vertical(g7)
    c: Coincident(g9,g5)
    c: Radius(g9) = 1.5
    c: Radius(g5) = 5
    c: Distance(g5,g-4) = 5
    c: DistanceX(g-2,g5) = 25
    c: Symmetric(g5,g6,g-4)
    c: Tangent(g10,g13) = 1.5708
    c: Tangent(g10,g12) = -1.5708
    c: Tangent(g12,g11) = -1.5708
    c: Tangent(g13,g11) = 1.5708
    c: Vertical(g12)
    c: Tangent(g14,g17) = 1.5708
    c: Tangent(g14,g16) = -1.5708
    c: Tangent(g16,g15) = -1.5708
    c: Tangent(g17,g15) = 1.5708
    c: Symmetric(g10,g11,g-3)
    c: Symmetric(g15,g14,g-3)
    c: Symmetric(g15,g11,g-2)
    c: Symmetric(g11,g15,g-2)
    c: Radius(g11) = 5
    c: Coincident(g18,g11)
    c: Coincident(g19,g15)
    c: Radius(g18) = 1.5
    c: Equal(g18,g19)
    c: Distance(g11,g-3) = 5
    c: DistanceX(g-2,g11) = -25
FEATURE [PartDesign::Pad] Pad012
  BaseFeature = -> Pad011
  Length = 2.5
  Length2 = 100
  Profile = -> Sketch016
  Reversed = true
  Type = 0
FEATURE [PartDesign::Chamfer] Chamfer
  Base = -> Pad012 [Edge299,Edge307,Edge338,Edge331,Edge332,Edge339,Edge302,Edge309]
  BaseFeature = -> Pad012
  Size = 1
FEATURE [PartDesign::Chamfer] Chamfer001
  Base = -> Chamfer [Edge358,Edge391,Edge371,Edge367]
  BaseFeature = -> Chamfer
  Size = 1
FEATURE [PartDesign::Chamfer] Chamfer002
  Base = -> Chamfer001 [Edge73,Edge74,Edge130,Edge128]
  BaseFeature = -> Chamfer001
  Size = 1
FEATURE [PartDesign::Body] Body  label="Boitier_dessous"
  Group = -> [Sketch,Pad,Fillet,Thickness,Sketch001,Pad001,Sketch007,Pocket,Sketch009,Pad008,Sketch013,Pocket002,Sketch014,Pocket003,Fillet001,Fillet002,Fillet003,Sketch015,Pad011,Sketch016,Pad012,Chamfer,Chamfer001,Chamfer002]
  Origin = -> Origin
  Tip = -> Chamfer002
FEATURE [Mesh::Feature] Mesh  label="Boitier_dessous (Meshed)"
FEATURE [Sketcher::SketchObject] Sketch017
  MapMode = 5
  Support = -> [XY_Plane003]
  sketch-geometry (8):
    g0: LineSegment StartX=-43 StartY=22 StartZ=0 EndX=-43 EndY=0 EndZ=0
    g1: LineSegment StartX=-43 StartY=0 StartZ=0 EndX=-36 EndY=0 EndZ=0
    g2: LineSegment StartX=-36 StartY=0 StartZ=0 EndX=-36 EndY=-41 EndZ=0
    g3: LineSegment StartX=-36 StartY=-41 StartZ=0 EndX=36 EndY=-41 EndZ=0
    g4: LineSegment StartX=36 StartY=-41 StartZ=0 EndX=36 EndY=0 EndZ=0
    g5: LineSegment StartX=36 StartY=0 StartZ=0 EndX=43 EndY=0 EndZ=0
    g6: LineSegment StartX=43 StartY=0 StartZ=0 EndX=43 EndY=22 EndZ=0
    g7: LineSegment StartX=43 StartY=22 StartZ=0 EndX=-43 EndY=22 EndZ=0
  constraints (22):
    c: Vertical(g0)
    c: Coincident(g0,g1)
    c: Horizontal(g1)
    c: Coincident(g1,g2)
    c: Vertical(g2)
    c: Coincident(g2,g3)
    c: Coincident(g3,g4)
    c: Vertical(g4)
    c: Coincident(g4,g5)
    c: Horizontal(g5)
    c: Coincident(g5,g6)
    c: Vertical(g6)
    c: Coincident(g6,g7)
    c: Coincident(g7,g0)
    c: Symmetric(g0,g6,g-2)
    c: Symmetric(g2,g3,g-2)
    c: DistanceX(g3,g3) = 72
    c: DistanceY(g4,g4) = 41
    c: Equal(g2,g4)
    c: DistanceX(g7,g7) = 86
    c: DistanceY(g6,g6) = 22
    c: PointOnObject(g1,g-1)
FEATURE [PartDesign::Pad] Pad013  label="Contours_boite001"
  Length = 2
  Length2 = 100
  Profile = -> Sketch017
  Type = 0
FEATURE [PartDesign::Fillet] Fillet004
  Base = -> Pad013 [Edge2,Edge5,Edge1,Edge8,Edge11,Edge14,Edge17,Edge20]
  BaseFeature = -> Pad013
  Radius = 3
FEATURE [PartDesign::Thickness] Thickness001
  Base = -> Fillet004 [Face2]
  BaseFeature = -> Fillet004
  Join = 0
  Mode = 0
  Value = 2.5
FEATURE [Sketcher::SketchObject] Sketch018
  ExternalGeometry = -> [Thickness001]
  MapMode = 5
  Placement = pos=(0,0,2) rot=(1,0,0;3.14159rad)
  Support = -> [Thickness001]
  sketch-geometry (20):
    g0: ArcOfCircle CenterX=-33 CenterY=38 CenterZ=0 NormalX=0 NormalY=0 NormalZ=1 AngleXU=0 Radius=4 StartAngle=1.5708 EndAngle=3.14159
    g1: LineSegment StartX=-33 StartY=42 StartZ=0 EndX=-31 EndY=42 EndZ=0
    g2: LineSegment StartX=-31 StartY=42 StartZ=0 EndX=-31 EndY=36 EndZ=0
    g3: LineSegment StartX=-31 StartY=36 StartZ=0 EndX=-37 EndY=36 EndZ=0
    g4: LineSegment StartX=-37 StartY=36 StartZ=0 EndX=-37 EndY=38 EndZ=0
    g5: ArcOfCircle CenterX=33 CenterY=38 CenterZ=0 NormalX=0 NormalY=0 NormalZ=1 AngleXU=0 Radius=4 StartAngle=0 EndAngle=1.5708
    g6: LineSegment StartX=33 StartY=42 StartZ=0 EndX=31 EndY=42 EndZ=0
    g7: LineSegment StartX=31 StartY=42 StartZ=0 EndX=31 EndY=36 EndZ=0
    g8: LineSegment StartX=31 StartY=36 StartZ=0 EndX=37 EndY=36 EndZ=0
    g9: LineSegment StartX=37 StartY=36 StartZ=0 EndX=37 EndY=38 EndZ=0
    g10: ArcOfCircle CenterX=40 CenterY=-19 CenterZ=0 NormalX=0 NormalY=0 NormalZ=1 AngleXU=0 Radius=4 StartAngle=4.71239 EndAngle=6.28319
    g11: LineSegment StartX=44 StartY=-19 StartZ=0 EndX=44 EndY=-17 EndZ=0
    g12: LineSegment StartX=44 StartY=-17 StartZ=0 EndX=38 EndY=-17 EndZ=0
    g13: LineSegment StartX=38 StartY=-17 StartZ=0 EndX=38 EndY=-23 EndZ=0
    g14: LineSegment StartX=38 StartY=-23 StartZ=0 EndX=40 EndY=-23 EndZ=0
    g15: ArcOfCircle CenterX=-40 CenterY=-19 CenterZ=0 NormalX=0 NormalY=0 NormalZ=1 AngleXU=0 Radius=4 StartAngle=3.14159 EndAngle=4.71239
    g16: LineSegment StartX=-44 StartY=-19 StartZ=0 EndX=-44 EndY=-17 EndZ=0
    g17: LineSegment StartX=-44 StartY=-17 StartZ=0 EndX=-38 EndY=-17 EndZ=0
    g18: LineSegment StartX=-38 StartY=-17 StartZ=0 EndX=-38 EndY=-23 EndZ=0
    g19: LineSegment StartX=-38 StartY=-23 StartZ=0 EndX=-40 EndY=-23 EndZ=0
  constraints (56):
    c: Coincident(g0,g-5)
    c: Tangent(g0,g1) = 1.5708
    c: Coincident(g1,g2)
    c: Vertical(g2)
    c: Coincident(g2,g3)
    c: Horizontal(g3)
    c: Coincident(g3,g4)
    c: Coincident(g4,g0)
    c: Vertical(g4)
    c: Radius(g0) = 4
    c: DistanceY(g2,g2) = 6
    c: DistanceX(g3,g3) = 6
    c: Horizontal(g1)
    c: Angle(g0) = 1.5708
    c: Coincident(g5,g-6)
    c: Tangent(g5,g6) = -1.5708
    c: Coincident(g6,g7)
    c: Vertical(g7)
    c: Coincident(g7,g8)
    c: Horizontal(g8)
    c: Coincident(g8,g9)
    c: Coincident(g9,g5)
    c: Vertical(g9)
    c: Radius(g5) = 4
    c: Angle(g5) = 1.5708
    c: Horizontal(g6)
    c: DistanceY(g7,g7) = 6
    c: DistanceX(g8,g8) = 6
    c: Coincident(g10,g-9)
    c: Tangent(g10,g11) = -1.5708
    c: Coincident(g11,g12)
    c: Horizontal(g12)
    c: Coincident(g12,g13)
    c: Vertical(g13)
    c: Coincident(g13,g14)
    c: Coincident(g14,g10)
    c: Horizontal(g14)
    c: Radius(g10) = 4
    c: Angle(g10) = 1.5708
    c: DistanceY(g13,g13) = 6
    c: DistanceX(g12,g12) = 6
    c: Vertical(g11)
    c: Coincident(g15,g-11)
    c: Tangent(g15,g16) = 1.5708
    c: Coincident(g16,g17)
    c: Horizontal(g17)
    c: Coincident(g17,g18)
    c: Vertical(g18)
    c: Coincident(g18,g19)
    c: Coincident(g19,g15)
    c: Horizontal(g19)
    c: Vertical(g16)
    c: Radius(g15) = 4
    c: Angle(g15) = 1.5708
    c: DistanceX(g17,g17) = 6
    c: DistanceY(g18,g18) = 6
FEATURE [PartDesign::Pad] Pad014  label="Supports_vis_fermeture"
  BaseFeature = -> Thickness001
  Length = 2
  Length2 = 100
  Profile = -> Sketch018
  Type = 0
FEATURE [Sketcher::SketchObject] Sketch019
  ExternalGeometry = -> [Pad014]
  MapMode = 5
  Placement = pos=(0,0,0) rot=(1,0,0;3.14159rad)
  Support = -> [Pad014]
  sketch-geometry (4):
    g0: Circle CenterX=-33.5 CenterY=38.5 CenterZ=0 NormalX=0 NormalY=0 NormalZ=1 AngleXU=0 Radius=1
    g1: Circle CenterX=33.5 CenterY=38.5 CenterZ=0 NormalX=0 NormalY=0 NormalZ=1 AngleXU=0 Radius=1
    g2: Circle CenterX=-40.5 CenterY=-19.5 CenterZ=0 NormalX=0 NormalY=0 NormalZ=1 AngleXU=0 Radius=1
    g3: Circle CenterX=40.5 CenterY=-19.5 CenterZ=0 NormalX=0 NormalY=0 NormalZ=1 AngleXU=0 Radius=1
  constraints (10):
    c: Distance(g1,g-6) = 2.5
    c: Distance(g1,g-5) = 2.5
    c: Symmetric(g1,g0,g-2)
    c: Symmetric(g2,g3,g-2)
    c: Distance(g2,g-10) = 2.5
    c: Distance(g2,g-9) = 2.5
    c: Radius(g2) = 1
    c: Equal(g2,g3)
    c: Equal(g2,g0)
    c: Equal(g2,g1)
FEATURE [PartDesign::Pocket] Pocket004
  BaseFeature = -> Pad014
  Length = 5
  Length2 = 100
  Profile = -> Sketch019
  Type = 0
FEATURE [PartDesign::Chamfer] Chamfer003
  Base = -> Pocket004 [Edge152,Edge153,Edge151,Edge61]
  BaseFeature = -> Pocket004
  Size = 1
FEATURE [Sketcher::SketchObject] Sketch020
  ExternalGeometry = -> [Chamfer003]
  MapMode = 5
  Placement = pos=(0,0,2) rot=(1,0,0;3.14159rad)
  Support = -> [Chamfer003]
  sketch-geometry (20):
    g0: LineSegment StartX=-31 StartY=41 StartZ=0 EndX=31 EndY=41 EndZ=0
    g1: LineSegment StartX=31 StartY=41 StartZ=0 EndX=31 EndY=40 EndZ=0
    g2: LineSegment StartX=31 StartY=40 StartZ=0 EndX=-31 EndY=40 EndZ=0
    g3: LineSegment StartX=-31 StartY=40 StartZ=0 EndX=-31 EndY=41 EndZ=0
    g4: LineSegment StartX=43 StartY=-3 StartZ=0 EndX=42 EndY=-3 EndZ=0
    g5: LineSegment StartX=42 StartY=-3 StartZ=0 EndX=42 EndY=-17 EndZ=0
    g6: LineSegment StartX=42 StartY=-17 StartZ=0 EndX=43 EndY=-17 EndZ=0
    g7: LineSegment StartX=43 StartY=-17 StartZ=0 EndX=43 EndY=-3 EndZ=0
    g8: LineSegment StartX=-43 StartY=-3 StartZ=0 EndX=-42 EndY=-3 EndZ=0
    g9: LineSegment StartX=-42 StartY=-3 StartZ=0 EndX=-42 EndY=-17 EndZ=0
    g10: LineSegment StartX=-42 StartY=-17 StartZ=0 EndX=-43 EndY=-17 EndZ=0
    g11: LineSegment StartX=-43 StartY=-17 StartZ=0 EndX=-43 EndY=-3 EndZ=0
    g12: LineSegment StartX=-38 StartY=-22 StartZ=0 EndX=38 EndY=-22 EndZ=0
    g13: LineSegment StartX=38 StartY=-22 StartZ=0 EndX=38 EndY=-21 EndZ=0
    g14: LineSegment StartX=38 StartY=-21 StartZ=0 EndX=-38 EndY=-21 EndZ=0
    g15: LineSegment StartX=-38 StartY=-21 StartZ=0 EndX=-38 EndY=-22 EndZ=0
    g16: LineSegment StartX=-36 StartY=36 StartZ=0 EndX=-35 EndY=36 EndZ=0
    g17: LineSegment StartX=-35 StartY=36 StartZ=0 EndX=-35 EndY=3 EndZ=0
    g18: LineSegment StartX=-35 StartY=3 StartZ=0 EndX=-36 EndY=3 EndZ=0
    g19: LineSegment StartX=-36 StartY=3 StartZ=0 EndX=-36 EndY=36 EndZ=0
  constraints (50):
    c: Coincident(g0,g1)
    c: Coincident(g1,g2)
    c: Coincident(g2,g3)
    c: Coincident(g3,g0)
    c: Horizontal(g2)
    c: Vertical(g1)
    c: Vertical(g3)
    c: Coincident(g0,g-3)
    c: Coincident(g0,g-3)
    c: Distance(g2,g0) = 1
    c: Coincident(g4,g5)
    c: Coincident(g5,g6)
    c: Coincident(g6,g7)
    c: Coincident(g7,g4)
    c: Horizontal(g4)
    c: Horizontal(g6)
    c: Vertical(g5)
    c: Coincident(g4,g-6)
    c: Coincident(g6,g-6)
    c: DistanceX(g4,g4) = 1
    c: Coincident(g8,g9)
    c: Coincident(g9,g10)
    c: Coincident(g10,g11)
    c: Coincident(g11,g8)
    c: Horizontal(g8)
    c: Horizontal(g10)
    c: Vertical(g9)
    c: Coincident(g8,g-5)
    c: Coincident(g10,g-5)
    c: DistanceX(g10,g10) = 1
    c: Coincident(g12,g13)
    c: Coincident(g13,g14)
    c: Coincident(g14,g15)
    c: Coincident(g15,g12)
    c: Horizontal(g14)
    c: Vertical(g13)
    c: Vertical(g15)
    c: Coincident(g12,g-7)
    c: Coincident(g12,g-7)
    c: DistanceY(g13,g13) = 1
    c: Coincident(g16,g17)
    c: Coincident(g17,g18)
    c: Coincident(g18,g19)
    c: Coincident(g19,g16)
    c: Horizontal(g16)
    c: Horizontal(g18)
    c: Vertical(g17)
    c: Coincident(g16,g-4)
    c: DistanceX(g18,g18) = 1
    c: Coincident(g18,g-4)
FEATURE [PartDesign::Pad] Pad015
  BaseFeature = -> Chamfer003
  Length = 4
  Length2 = 100
  Profile = -> Sketch020
  Type = 0
FEATURE [Sketcher::SketchObject] Sketch021
  ExternalGeometry = -> [Pad015]
  MapMode = 5
  Placement = pos=(0,0,2) rot=(1,0,0;3.14159rad)
  Support = -> [Pad015]
  sketch-geometry (8):
    g0: ArcOfCircle CenterX=-28 CenterY=32 CenterZ=0 NormalX=0 NormalY=0 NormalZ=1 AngleXU=0 Radius=3 StartAngle=1.5708 EndAngle=3.14159
    g1: ArcOfCircle CenterX=28 CenterY=32 CenterZ=0 NormalX=0 NormalY=0 NormalZ=1 AngleXU=0 Radius=3 StartAngle=1e-16 EndAngle=1.5708
    g2: ArcOfCircle CenterX=28 CenterY=3 CenterZ=0 NormalX=0 NormalY=0 NormalZ=1 AngleXU=0 Radius=3 StartAngle=4.71239 EndAngle=6.28319
    g3: ArcOfCircle CenterX=-28 CenterY=3 CenterZ=0 NormalX=0 NormalY=0 NormalZ=1 AngleXU=0 Radius=3 StartAngle=3.14159 EndAngle=4.71239
    g4: LineSegment StartX=-31 StartY=32 StartZ=0 EndX=-31 EndY=3 EndZ=0
    g5: LineSegment StartX=31 StartY=32 StartZ=0 EndX=31 EndY=3 EndZ=0
    g6: LineSegment StartX=-28 StartY=35 StartZ=0 EndX=28 EndY=35 EndZ=0
    g7: LineSegment StartX=-28 StartY=0 StartZ=0 EndX=28 EndY=0 EndZ=0
  constraints (23):
    c: PointOnObject(g3,g-1)
    c: Radius(g0) = 3
    c: Equal(g0,g1)
    c: Equal(g0,g2)
    c: Equal(g0,g3)
    c: Angle(g0) = 1.5708
    c: Angle(g1) = 1.5708
    c: Angle(g2) = 1.5708
    c: Angle(g3) = 1.5708
    c: Vertical(g4)
    c: Tangent(g4,g0) = -1.5708
    c: Tangent(g4,g3) = -1.5708
    c: Tangent(g5,g1) = 1.5708
    c: Tangent(g5,g2) = 1.5708
    c: Vertical(g5)
    c: Coincident(g6,g0)
    c: Coincident(g6,g1)
    c: Horizontal(g6)
    c: Coincident(g7,g3)
    c: Coincident(g7,g2)
    c: Symmetric(g3,g2,g-2)
    c: Distance(g1,g-8) = 5
    c: Distance(g-9,g6) = 5
FEATURE [PartDesign::Pocket] Pocket005
  BaseFeature = -> Pad015
  Length = 2
  Length2 = 100
  Profile = -> Sketch021
  Type = 0
FEATURE [PartDesign::Body] Body003  label="Boitier_dessus"
  Group = -> [Pad013,Sketch017,Fillet004,Thickness001,Sketch018,Pad014,Sketch019,Pocket004,Chamfer003,Sketch020,Pad015,Sketch021,Pocket005]
  Origin = -> Origin003
  Placement = pos=(0,0,26) rot=(0,0,1;0rad)
  Tip = -> Pocket005
FEATURE [Mesh::Feature] Mesh001  label="Boitier_dessus (Meshed)"
